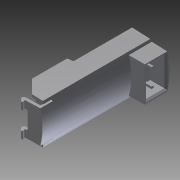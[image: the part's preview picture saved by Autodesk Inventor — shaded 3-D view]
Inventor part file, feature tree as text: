
AUTODESK INVENTOR PART (.ipt)
format: ipt  version: 2014 (Build 180170000, 170)  size: 401,920 bytes
history: native  units: mm
features: sketch x26, extrude x22, other x14, revolve x4
ambient origin geometry x8: Origin, YZ Plane, XZ Plane, XY Plane, X Axis, Y Axis, Z Axis, Center Point
bodies: Solid1 (feature_tree)
feature tree (66):
  extrude  "Extrusion1"  Depth=10.0mm TaperAngle=0.0deg
  sketch  "Sketch_1"  dims[d0=10.0mm d1=0.0mm d2=2.0mm d3=0.0mm]
  sketch  "Sketch_3"  dims[d7=0.77mm d8=0.0mm d9=0.77mm d10=0.0mm]
  extrude  "Extrusion2"  Depth=7.0mm TaperAngle=0.0deg
  revolve  "Revolution1"  [1 undecoded]
  sketch  "Sketch_6"  dims[d19=30.0mm d20=0.0mm d21=5.0mm d22=0.0mm]
  sketch  "Sketch_7"  dims[d23=35.0mm d24=0.0mm d25=1.5mm d26=0.0mm]
  extrude  "Extrusion3"  Depth=10.0mm TaperAngle=0.0deg
  extrude  "Extrusion4"  Depth=0.512mm TaperAngle=0.0deg
  extrude  "Extrusion5"  Depth=5.0mm TaperAngle=0.0deg
  extrude  "Extrusion6"  Depth=1.5mm TaperAngle=0.0deg
  extrude  "Extrusion7"  Depth=6.0mm
  extrude  "Extrusion8"  Depth=2.0mm TaperAngle=45.0deg
  extrude  "Extrusion9"  Depth=3.25mm TaperAngle=0.0deg
  extrude  "Extrusion10"  Depth=1.05mm
  extrude  "Extrusion11"  TaperAngle=360.0deg  [1 undecoded]
  extrude  "Extrusion12"  Depth=1.722mm TaperAngle=0.0deg
  extrude  "Extrusion13"  [1 undecoded]
  extrude  "Extrusion14"  [1 undecoded]
  extrude  "Extrusion15"  [1 undecoded]
  revolve  "Revolution2"  [1 undecoded]
  extrude  "Extrusion16"  [1 undecoded]
  extrude  "Extrusion17"  [1 undecoded]
  extrude  "Extrusion18"  [1 undecoded]
  extrude  "Extrusion19"  [1 undecoded]
  extrude  "Extrusion20"  [1 undecoded]
  extrude  "Extrusion21"  [1 undecoded]
  revolve  "Revolution3"  [1 undecoded]
  revolve  "Revolution4"  [1 undecoded]
  extrude  "Extrusion22"  [1 undecoded]
  other  "NEBV_XY"
  other  "NEBV_YZ"
  other  "NEBV_ZX"
  other  "NEBV_X"
  other  "NEBV_Y"
  other  "NEBV_Z"
  other  "NEBV_Center"
  other  "VAVE_XY"
  other  "VAVE_YZ"
  other  "VAVE_ZX"
  other  "VAVE_X"
  other  "VAVE_Y"
  other  "VAVE_Z"
  other  "VAVE_Center"
  sketch  "Sketch_23"
  sketch  "Sketch_4"  dims[d11=3.062mm d12=0.0mm d13=10.0mm d14=0.0mm]
  sketch  "Sketch_5"  dims[d15=0.512mm d16=0.0mm d17=0.512mm d18=0.0mm]
  sketch  "Sketch_12"  dims[d42=1.05mm d43=-0.174533mm d44=360.0deg]
  sketch  "Sketch_8"  dims[d27=0.3mm d28=0.0mm d29=6.0mm d30=0.174533mm]
  sketch  "Sketch_9"  dims[d31=6.981317mm d32=2.0mm d33=45.0deg]
  sketch  "Sketch_10"  dims[d34=3.38mm d35=0.0mm d36=3.25mm d37=0.0mm]
  sketch  "Sketch_15"
  sketch  "Sketch_13"  dims[d45=360.0deg d46=1.722mm d47=0.0mm]
  sketch  "Sketch_14"
  sketch  "Sketch_17"
  sketch  "Sketch_11"  dims[d38=3.25mm d39=0.0mm d40=1.05mm d41=-0.174533mm]
  sketch  "Sketch_16"
  sketch  "Sketch_19"
  sketch  "Sketch_20"
  sketch  "Sketch_21"
  sketch  "Sketch_22"
  sketch  "Sketch_2"  dims[d4=60.0deg d5=7.0mm d6=0.0mm]
  sketch  "Sketch_24"
  sketch  "Sketch_25"
  sketch  "Sketch_26"
  sketch  "Sketch_40"
note: 15 required parameter values undecoded (feature->parameter linkage not recoverable at this tier; creation-order binding heuristic only, values carry confidence <= 0.55)